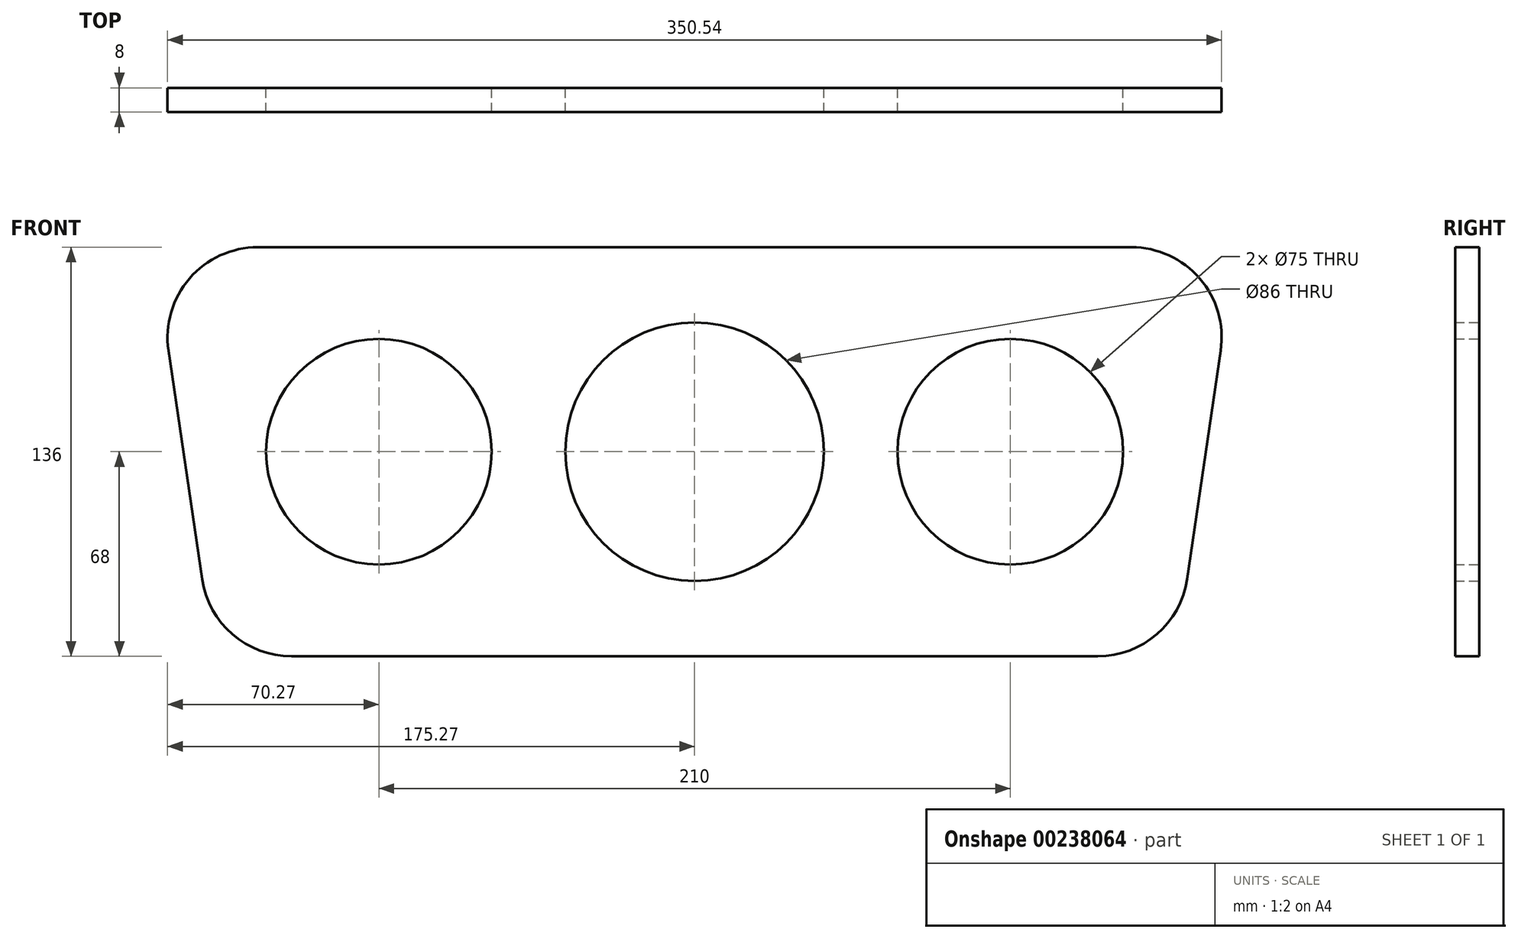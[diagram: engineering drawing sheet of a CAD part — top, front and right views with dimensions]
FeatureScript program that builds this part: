
annotation { "Feature Type Name" : "Feature", "Feature Type Description" : "" }
export const myFeature = defineFeature(function(context is Context, id is Id, definition is map)
    precondition{}
    {
        {
            var Q0;
            Q0=qCreatedBy(makeId("Front.planeOp"),FACE);
            var sketch = newSketch(context, id + "F0", { "sketchPlane" : qUnion([Q0])});
            skLineSegment(sketch, "E0", {"start": v(0, 0) * mm, "end": v(-145.27, 0) * mm});
            skLineSegment(sketch, "E1", {"start": v(-174.95, -34.36) * mm, "end": v(-163.77, -110.36) * mm});
            skLineSegment(sketch, "E2", {"start": v(-134.09, -136) * mm, "end": v(0, -136) * mm});
            skPoint(sketch, "E3.visualSharp", {"position": v(-180, 0) * mm});
            skArc(sketch, "E3.filletArc", {"start": v(-145.27, 0) * mm, "mid": v(-167.97, -10.4) * mm, "end": v(-174.95, -34.36) * mm});
            skPoint(sketch, "E4.visualSharp", {"position": v(-160, -136) * mm});
            skArc(sketch, "E4.filletArc", {"start": v(-163.77, -110.36) * mm, "mid": v(-153.7, -128.7) * mm, "end": v(-134.09, -136) * mm});
            skLineSegment(sketch, "E5.MirrorCS", {"start": v(0, 0) * mm, "end": v(145.27, 0) * mm});
            skArc(sketch, "E6.MirrorCS", {"start": v(145.27, 0) * mm, "mid": v(167.97, -10.4) * mm, "end": v(174.95, -34.36) * mm});
            skLineSegment(sketch, "E7.MirrorCS", {"start": v(174.95, -34.36) * mm, "end": v(163.77, -110.36) * mm});
            skArc(sketch, "E8.MirrorCS", {"start": v(163.77, -110.36) * mm, "mid": v(153.7, -128.7) * mm, "end": v(134.09, -136) * mm});
            skLineSegment(sketch, "E9.MirrorCS", {"start": v(134.09, -136) * mm, "end": v(0, -136) * mm});
            skCircle(sketch, "E10", {"center": v(0, -68) * mm, "radius": 43 * mm});
            skCircle(sketch, "E11", {"center": v(-105, -68) * mm, "radius": 37.5 * mm});
            skCircle(sketch, "E12.MirrorC", {"center": v(105, -68) * mm, "radius": 37.5 * mm});
            skSolve(sketch);
        }
        {
            var Q0;
            Q0=makeQuery(id+"F0.imprint","IMPRINT",FACE,{"disambiguationData":[TD([[makeQuery(id+"F0.imprint","IMPRINT",EDGE,{"derivedFrom":sQuery(id+"F0.wireOp",EDGE,"E0")}),1.0]])]});
            extrude(context, id + "F1", {"entities" : qUnion([Q0]), "depth" : 8 * mm});
        }
    });
